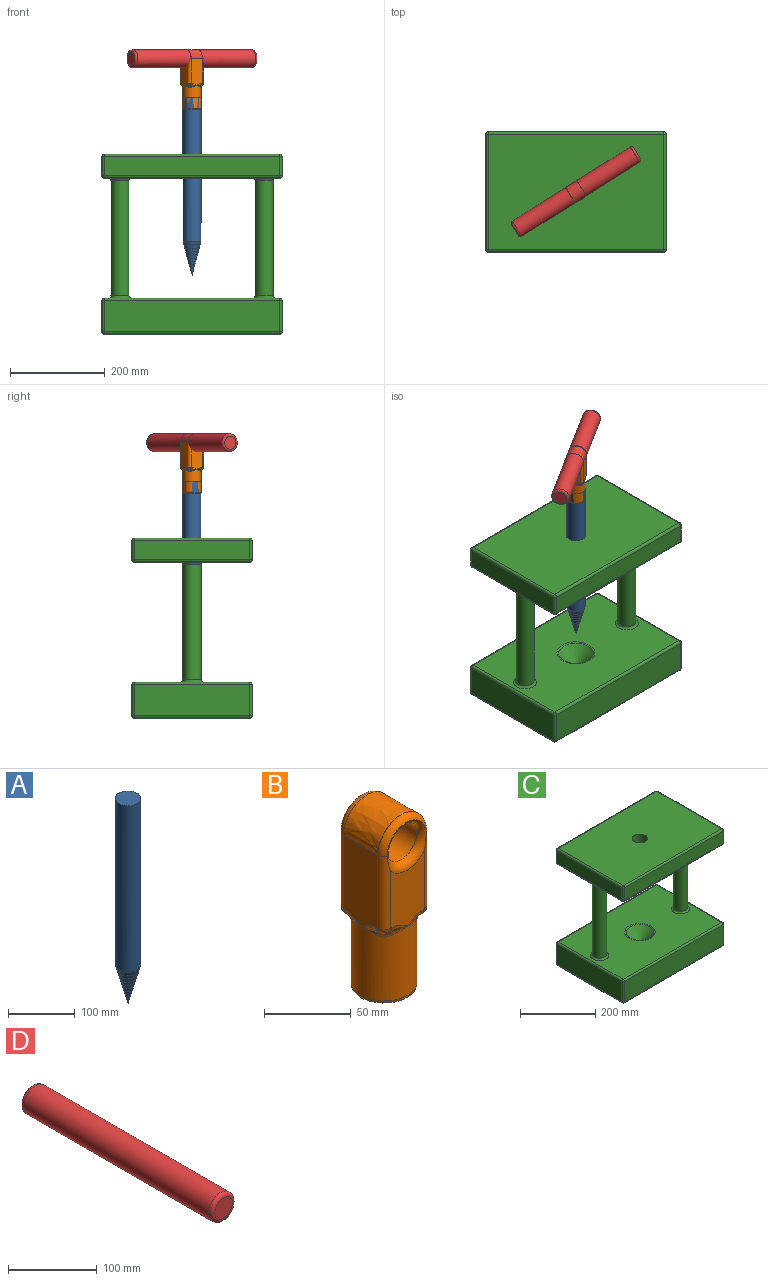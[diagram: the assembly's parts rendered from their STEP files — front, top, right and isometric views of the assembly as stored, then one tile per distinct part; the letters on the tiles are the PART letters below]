
ASSEMBLY  parts=4 mates=3
PART A: 8 faces, bbox 38.1x38.1x375.9 mm
  f0: cylinder r=19.05mm len=304.8mm, axis (0,0,-1), area 36482.9mm2, adj f1,f2
  f1: plane 38.1x38.1mm, normal (0,0,1), area 1140.1mm2, adj f0
  f2: cone r=19.05mm half-angle=15deg, axis (0,0,1), area 4405mm2, adj f0,f4,f5,f6,f7
  f3: plane 0.12x0.07mm, normal (0,-1,0), area 0mm2, adj f5,f6,f7
  f4: plane 0.04x0.01mm, normal (1,0.02,0), area 0mm2, adj f2,f6,f7
  f5: bspline ~71.21x37.26mm, area 79.7mm2, adj f2,f3,f6,f7
  f6: bspline ~71.21x37.27mm, area 69mm2, adj f2,f3,f4,f5,f7
  f7: bspline ~71.1x37.27mm, area 40.3mm2, adj f2,f3,f4,f5,f6
PART B: 95 faces, bbox 50.4x45.4x137.3 mm
  f0: plane 58.32x29.11mm, normal (-1,0,0), area 1503.6mm2, adj f2,f17,f19,f20,f22,f24,f26
  f1: plane 61.29x32.08mm, normal (1,0,0), area 1503.6mm2, adj f2,f8,f10,f12,f29,f30,f31
  f2: extruded ~38.1x27.94mm, area 1672.1mm2, adj f0,f1,f15,f28
  f3: plane 46.15x27.94mm, normal (0,-1,0), area 1064.2mm2, adj f21,f23,f26,f27,f30,f33,f34
  f4: plane 46.15x27.94mm, normal (0,1,0), area 1064.2mm2, adj f7,f9,f12,f13,f14,f16,f17
  f5: cylinder r=12.7mm len=27.94mm, axis (0,-1,0), area 2229.5mm2, adj f14,f27
  f6: cylinder r=19.05mm len=49.21mm, axis (0,0,1), area 5649.1mm2, adj f74,f75,f76,f77,f78,f79,f80,f81
  f7: bspline ~13.58x5.44mm, area 19.6mm2, adj f4,f9,f79
  f8: bspline ~13.58x5.42mm, area 19.6mm2, adj f1,f10,f82
  f9: cylinder r=5.08mm len=4.2mm, axis (1,0,0), area 4.8mm2, adj f4,f7,f11,f80
  f10: cylinder r=5.08mm len=4.2mm, axis (0,-1,0), area 4.8mm2, adj f1,f8,f11,f83
  f11: sphere r=5.08mm, area 35.7mm2, adj f9,f10,f12,f81
  f12: cylinder r=5.08mm len=52.07mm, axis (0,0,1), area 404.8mm2, adj f1,f4,f11,f14,f15
  f13: bspline ~13.58x5.44mm, area 2.1mm2, adj f4,f16,f92
  f14: torus R=17.78mm, axis (0,-1,0), area 603.8mm2, adj f4,f5,f12,f15,f17
  f15: bspline ~38.1x28.37mm, area 339.7mm2, adj f2,f12,f14,f17
  f16: cylinder r=5.08mm len=4.2mm, axis (1,0,0), area 4.8mm2, adj f4,f13,f18,f93
  f17: cylinder r=5.08mm len=52.07mm, axis (0,0,-1), area 404.8mm2, adj f0,f4,f14,f15,f18
  f18: sphere r=5.08mm, area 33.5mm2, adj f16,f17,f19,f91
  f19: cylinder r=5.08mm len=4.2mm, axis (0,1,0), area 4.8mm2, adj f0,f18,f20,f90
  f20: bspline ~13.58x5.44mm, area 19.5mm2, adj f0,f19,f89
  f21: bspline ~13.58x5.42mm, area 19.6mm2, adj f3,f23,f74
  f22: bspline ~13.58x5.44mm, area 19.5mm2, adj f0,f24,f77
  f23: cylinder r=5.08mm len=4.2mm, axis (-1,0,0), area 4.8mm2, adj f3,f21,f25,f75
  f24: cylinder r=5.08mm len=4.2mm, axis (0,1,0), area 4.8mm2, adj f0,f22,f25,f78
  f25: sphere r=5.08mm, area 33.5mm2, adj f23,f24,f26,f76
  f26: cylinder r=5.08mm len=52.07mm, axis (0,0,1), area 404.8mm2, adj f0,f3,f25,f27,f28
  f27: torus R=17.78mm, axis (0,-1,0), area 603.8mm2, adj f3,f5,f26,f28,f30
  f28: bspline ~38.1x28.37mm, area 339.7mm2, adj f2,f26,f27,f30
  f29: bspline ~13.58x5.42mm, area 18.8mm2, adj f1,f31,f84
  f30: cylinder r=5.08mm len=52.07mm, axis (0,0,-1), area 404.8mm2, adj f1,f3,f27,f28,f32
  f31: cylinder r=5.08mm len=4.2mm, axis (0,-1,0), area 4.8mm2, adj f1,f29,f32,f85
  f32: sphere r=5.08mm, area 35.7mm2, adj f30,f31,f33,f86
  f33: cylinder r=5.08mm len=4.2mm, axis (-1,0,0), area 4.8mm2, adj f3,f32,f34,f88
  f34: bspline ~13.58x5.42mm, area 19.6mm2, adj f3,f33,f87
  f35: plane 1.72x1.72mm, normal (0,0,1), area 0.9mm2, adj f45,f52,f55,f58,f59
  f36: plane 1.64x1.64mm, normal (0,0,1), area 0.9mm2, adj f45,f46,f47,f48,f49
  f37: plane 1.72x1.72mm, normal (0,0,1), area 0.9mm2, adj f45,f68,f70,f72,f73
  f38: plane 57.15x27.94mm, normal (1,0,0), area 1503.6mm2, adj f41,f56,f58,f59,f61,f63,f65
  f39: plane 1.64x1.64mm, normal (0,0,1), area 0.9mm2, adj f45,f60,f61,f62,f63
  f40: plane 57.15x27.94mm, normal (-1,0,0), area 1503.6mm2, adj f41,f47,f49,f51,f68,f69,f70
  f41: extruded ~37.59x27.94mm, area 1649.8mm2, adj f38,f40,f54,f67
  f42: plane 46.15x27.94mm, normal (0,1,0), area 1064.2mm2, adj f60,f62,f65,f66,f69,f72,f73
  f43: plane 46.15x27.94mm, normal (0,-1,0), area 1064.2mm2, adj f46,f48,f51,f52,f53,f55,f56
  f44: cylinder r=12.95mm len=27.94mm, axis (0,-1,0), area 2274.1mm2, adj f53,f66
  f45: cylinder r=18.8mm len=51.05mm, axis (0,0,1), area 6015.5mm2, adj f35,f36,f37,f39,f46,f47,f52,f59
  f46: bspline ~13.58x5.17mm, area 47.8mm2, adj f36,f43,f45,f48
  f47: bspline ~13.58x5.15mm, area 47.8mm2, adj f36,f40,f45,f49
  f48: cylinder r=4.83mm len=4.83mm, axis (1,0,0), area 7.7mm2, adj f36,f43,f46,f50
  f49: cylinder r=4.83mm len=4.83mm, axis (0,-1,0), area 7.7mm2, adj f36,f40,f47,f50
  f50: sphere r=4.83mm, area 36.6mm2, adj f48,f49,f51
  f51: cylinder r=4.83mm len=52.07mm, axis (0,0,1), area 384mm2, adj f40,f43,f50,f53,f54
  f52: bspline ~13.11x5.08mm, area 47.8mm2, adj f35,f43,f45,f55
  f53: torus R=17.78mm, axis (0,-1,0), area 574.7mm2, adj f43,f44,f51,f54,f56
  f54: bspline ~37.59x28.12mm, area 314mm2, adj f41,f51,f53,f56
  f55: cylinder r=4.83mm len=4.83mm, axis (1,0,0), area 7.7mm2, adj f35,f43,f52,f57
  f56: cylinder r=4.83mm len=52.07mm, axis (0,0,-1), area 384mm2, adj f38,f43,f53,f54,f57
  f57: sphere r=4.83mm, area 49.9mm2, adj f55,f56,f58
  f58: cylinder r=4.83mm len=4.83mm, axis (0,1,0), area 7.7mm2, adj f35,f38,f57,f59
  f59: bspline ~13.58x5.17mm, area 47.8mm2, adj f35,f38,f45,f58
  f60: bspline ~13.58x5.15mm, area 47.8mm2, adj f39,f42,f45,f62
  f61: bspline ~13.58x5.17mm, area 47.8mm2, adj f38,f39,f45,f63
  f62: cylinder r=4.83mm len=4.83mm, axis (-1,0,0), area 7.7mm2, adj f39,f42,f60,f64
  f63: cylinder r=4.83mm len=4.83mm, axis (0,1,0), area 7.7mm2, adj f38,f39,f61,f64
  f64: sphere r=4.83mm, area 36.6mm2, adj f62,f63,f65
  f65: cylinder r=4.83mm len=52.07mm, axis (0,0,1), area 384mm2, adj f38,f42,f64,f66,f67
  f66: torus R=17.78mm, axis (0,-1,0), area 574.7mm2, adj f42,f44,f65,f67,f69
  f67: bspline ~37.59x28.12mm, area 314mm2, adj f41,f65,f66,f69
  f68: bspline ~13.58x5.15mm, area 47.8mm2, adj f37,f40,f45,f70
  f69: cylinder r=4.83mm len=52.07mm, axis (0,0,-1), area 384mm2, adj f40,f42,f66,f67,f71
  f70: cylinder r=4.83mm len=4.83mm, axis (0,-1,0), area 7.7mm2, adj f37,f40,f68,f71
  f71: sphere r=4.83mm, area 36.6mm2, adj f69,f70,f72
  f72: cylinder r=4.83mm len=4.83mm, axis (-1,0,0), area 7.7mm2, adj f37,f42,f71,f73
  f73: bspline ~13.58x5.15mm, area 47.7mm2, adj f37,f42,f45,f72
  f74: bspline ~13.17x4.09mm, area 26.5mm2, adj f6,f21,f75
  f75: bspline ~7.38x5.9mm, area 5.6mm2, adj f6,f23,f74,f76
  f76: bspline ~7.24x6.66mm, area 28.6mm2, adj f6,f25,f75,f78
  f77: bspline ~13.24x4.11mm, area 18.4mm2, adj f6,f22,f78
  f78: bspline ~7.38x5.9mm, area 5.6mm2, adj f6,f24,f76,f77
  f79: bspline ~13.17x4.09mm, area 18.9mm2, adj f6,f7,f80
  f80: bspline ~7.38x5.9mm, area 5.6mm2, adj f6,f9,f79,f81
  f81: bspline ~7.63x7.63mm, area 28.6mm2, adj f6,f11,f80,f83
  f82: bspline ~13.24x4.11mm, area 18.4mm2, adj f6,f8,f83
  f83: bspline ~7.38x5.9mm, area 5.6mm2, adj f6,f10,f81,f82
  f84: bspline ~13.07x4.07mm, area 18.6mm2, adj f6,f29,f85
  f85: bspline ~7.38x5.9mm, area 5.6mm2, adj f6,f31,f84,f86
  f86: bspline ~7.24x6.66mm, area 28.6mm2, adj f6,f32,f85,f88
  f87: bspline ~13.24x4.11mm, area 26.5mm2, adj f6,f34,f88
  f88: bspline ~7.38x5.9mm, area 5.6mm2, adj f6,f33,f86,f87
  f89: bspline ~13.07x4.07mm, area 18.4mm2, adj f6,f20,f90
  f90: bspline ~7.38x5.9mm, area 5.6mm2, adj f6,f19,f89,f91
  f91: bspline ~7.63x7.63mm, area 28.6mm2, adj f6,f18,f90,f93
  f92: bspline ~12.95x4.05mm, area 18.7mm2, adj f6,f13,f93
  f93: bspline ~7.38x5.9mm, area 5.6mm2, adj f6,f16,f91,f92
  f94: torus R=13.97mm, axis (0,0,-1), area 192.2mm2, adj f6,f45
PART C: 62 faces, bbox 381x254x381 mm
  f0: plane 370.84x66.04mm, normal (0,1,0), area 24490.3mm2, adj f44,f49,f52,f55
  f1: plane 243.84x66.04mm, normal (-1,0,0), area 16103.2mm2, adj f41,f50,f51,f55
  f2: plane 370.84x66.04mm, normal (0,-1,0), area 24490.3mm2, adj f36,f40,f41,f42
  f3: plane 243.84x66.04mm, normal (1,0,0), area 16103.2mm2, adj f36,f39,f43,f44
  f4: plane 370.84x243.84mm, normal (0,0,1), area 81689.2mm2, adj f39,f40,f49,f50,f56,f57,f58
  f5: plane 370.84x243.84mm, normal (0,0,-1), area 90425.6mm2, adj f42,f43,f51,f52
  f6: cone r=38.1mm half-angle=45deg, axis (0,0,1), area 5955.4mm2, adj f58
  f7: cylinder r=19.05mm len=243.84mm, axis (0,0,-1), area 29186.4mm2, adj f57,f61
  f8: cylinder r=19.05mm len=243.84mm, axis (0,0,-1), area 29186.4mm2, adj f56,f60
  f9: plane 370.84x243.84mm, normal (0,0,-1), area 84740.4mm2, adj f18,f19,f30,f34,f59,f60,f61
  f10: plane 370.84x40.64mm, normal (0,1,0), area 15070.9mm2, adj f28,f29,f33,f34
  f11: plane 243.84x40.64mm, normal (-1,0,0), area 9909.7mm2, adj f24,f25,f29,f30
  f12: plane 370.84x40.64mm, normal (0,-1,0), area 15070.9mm2, adj f16,f19,f22,f25
  f13: plane 243.84x40.64mm, normal (1,0,0), area 9909.7mm2, adj f17,f18,f22,f33
  f14: plane 370.84x243.84mm, normal (0,0,1), area 89128.5mm2, adj f15,f16,f17,f24,f28
  f15: cylinder r=20.32mm len=45.72mm, axis (0,0,1), area 5837.3mm2, adj f14,f59
  f16: cylinder r=5.08mm len=370.84mm, axis (-1,0,0), area 2959.2mm2, adj f12,f14,f20,f23
  f17: cylinder r=5.08mm len=243.84mm, axis (0,-1,0), area 1945.8mm2, adj f13,f14,f20,f31
  f18: cylinder r=5.08mm len=243.84mm, axis (0,1,0), area 1945.8mm2, adj f9,f13,f21,f35
  f19: cylinder r=5.08mm len=370.84mm, axis (1,0,0), area 2959.2mm2, adj f9,f12,f21,f27
  f20: sphere r=5.08mm, area 40.5mm2, adj f16,f17,f22
  f21: sphere r=5.08mm, area 40.5mm2, adj f18,f19,f22
  f22: cylinder r=5.08mm len=40.64mm, axis (0,0,1), area 324.3mm2, adj f12,f13,f20,f21
  f23: sphere r=5.08mm, area 40.5mm2, adj f16,f24,f25
  f24: cylinder r=5.08mm len=243.84mm, axis (0,1,0), area 1945.8mm2, adj f11,f14,f23,f26
  f25: cylinder r=5.08mm len=40.64mm, axis (0,0,-1), area 324.3mm2, adj f11,f12,f23,f27
  f26: sphere r=5.08mm, area 40.5mm2, adj f24,f28,f29
  f27: sphere r=5.08mm, area 40.5mm2, adj f19,f25,f30
  f28: cylinder r=5.08mm len=370.84mm, axis (1,0,0), area 2959.2mm2, adj f10,f14,f26,f31
  f29: cylinder r=5.08mm len=40.64mm, axis (0,0,1), area 324.3mm2, adj f10,f11,f26,f32
  f30: cylinder r=5.08mm len=243.84mm, axis (0,-1,0), area 1945.8mm2, adj f9,f11,f27,f32
  f31: sphere r=5.08mm, area 40.5mm2, adj f17,f28,f33
  f32: sphere r=5.08mm, area 40.5mm2, adj f29,f30,f34
  f33: cylinder r=5.08mm len=40.64mm, axis (0,0,-1), area 324.3mm2, adj f10,f13,f31,f35
  f34: cylinder r=5.08mm len=370.84mm, axis (-1,0,0), area 2959.2mm2, adj f9,f10,f32,f35
  f35: sphere r=5.08mm, area 40.5mm2, adj f18,f33,f34
  f36: cylinder r=5.08mm len=66.04mm, axis (0,0,1), area 527mm2, adj f2,f3,f37,f38
  f37: sphere r=5.08mm, area 40.5mm2, adj f36,f39,f40
  f38: sphere r=5.08mm, area 40.5mm2, adj f36,f42,f43
  f39: cylinder r=5.08mm len=243.84mm, axis (0,-1,0), area 1945.8mm2, adj f3,f4,f37,f45
  f40: cylinder r=5.08mm len=370.84mm, axis (-1,0,0), area 2959.2mm2, adj f2,f4,f37,f46
  f41: cylinder r=5.08mm len=66.04mm, axis (0,0,-1), area 527mm2, adj f1,f2,f46,f47
  f42: cylinder r=5.08mm len=370.84mm, axis (1,0,0), area 2959.2mm2, adj f2,f5,f38,f47
  f43: cylinder r=5.08mm len=243.84mm, axis (0,1,0), area 1945.8mm2, adj f3,f5,f38,f48
  f44: cylinder r=5.08mm len=66.04mm, axis (0,0,-1), area 527mm2, adj f0,f3,f45,f48
  f45: sphere r=5.08mm, area 40.5mm2, adj f39,f44,f49
  f46: sphere r=5.08mm, area 40.5mm2, adj f40,f41,f50
  f47: sphere r=5.08mm, area 40.5mm2, adj f41,f42,f51
  f48: sphere r=5.08mm, area 40.5mm2, adj f43,f44,f52
  f49: cylinder r=5.08mm len=370.84mm, axis (1,0,0), area 2959.2mm2, adj f0,f4,f45,f53
  f50: cylinder r=5.08mm len=243.84mm, axis (0,1,0), area 1945.8mm2, adj f1,f4,f46,f53
  f51: cylinder r=5.08mm len=243.84mm, axis (0,-1,0), area 1945.8mm2, adj f1,f5,f47,f54
  f52: cylinder r=5.08mm len=370.84mm, axis (-1,0,0), area 2959.2mm2, adj f0,f5,f48,f54
  f53: sphere r=5.08mm, area 40.5mm2, adj f49,f50,f55
  f54: sphere r=5.08mm, area 40.5mm2, adj f51,f52,f55
  f55: cylinder r=5.08mm len=66.04mm, axis (0,0,1), area 527mm2, adj f0,f1,f53,f54
  f56: torus R=24.13mm, axis (0,0,1), area 1047.7mm2, adj f4,f8
  f57: torus R=24.13mm, axis (0,0,1), area 1047.7mm2, adj f4,f7
  f58: torus R=40.2mm, axis (0,0,1), area 960.4mm2, adj f4,f6
  f59: torus R=25.4mm, axis (0,0,1), area 1111.3mm2, adj f9,f15
  f60: torus R=24.13mm, axis (0,0,1), area 1047.7mm2, adj f8,f9
  f61: torus R=24.13mm, axis (0,0,1), area 1047.7mm2, adj f7,f9
PART D: 5 faces, bbox 39.1x304.8x39.1 mm
  f0: cylinder r=19.05mm len=294.64mm, axis (0,1,0), area 35266.8mm2, adj f3,f4
  f1: plane 27.95x27.95mm, normal (0,-1,0), area 613.1mm2, adj f3
  f2: plane 27.95x27.95mm, normal (0,1,0), area 613.1mm2, adj f4
  f3: bspline ~39.09x39.09mm, area 899mm2, adj f0,f1
  f4: bspline ~39.09x39.09mm, area 899mm2, adj f0,f2
PLACE A rot(axis=(0,0,-1),57.8deg) t=(0,0,158.44)mm
PLACE B rot(axis=(0,0,-1),57.8deg) t=(16.12,10.15,516.27)mm
PLACE C at identity fixed
PLACE D rot(axis=(0,0,-1),57.8deg) t=(0,0,544.85)mm
MATE cylindrical C.f15 <-> A.f0  axis (0,0,1) through (0,0,342.9)mm
MATE fastened D.f0 <-> B.f5  axis (0.85,0.53,0) through (0,0,544.85)mm
MATE fastened B.f6 <-> A.f0  axis (0,0,1) through (0,0,463.24)mm
